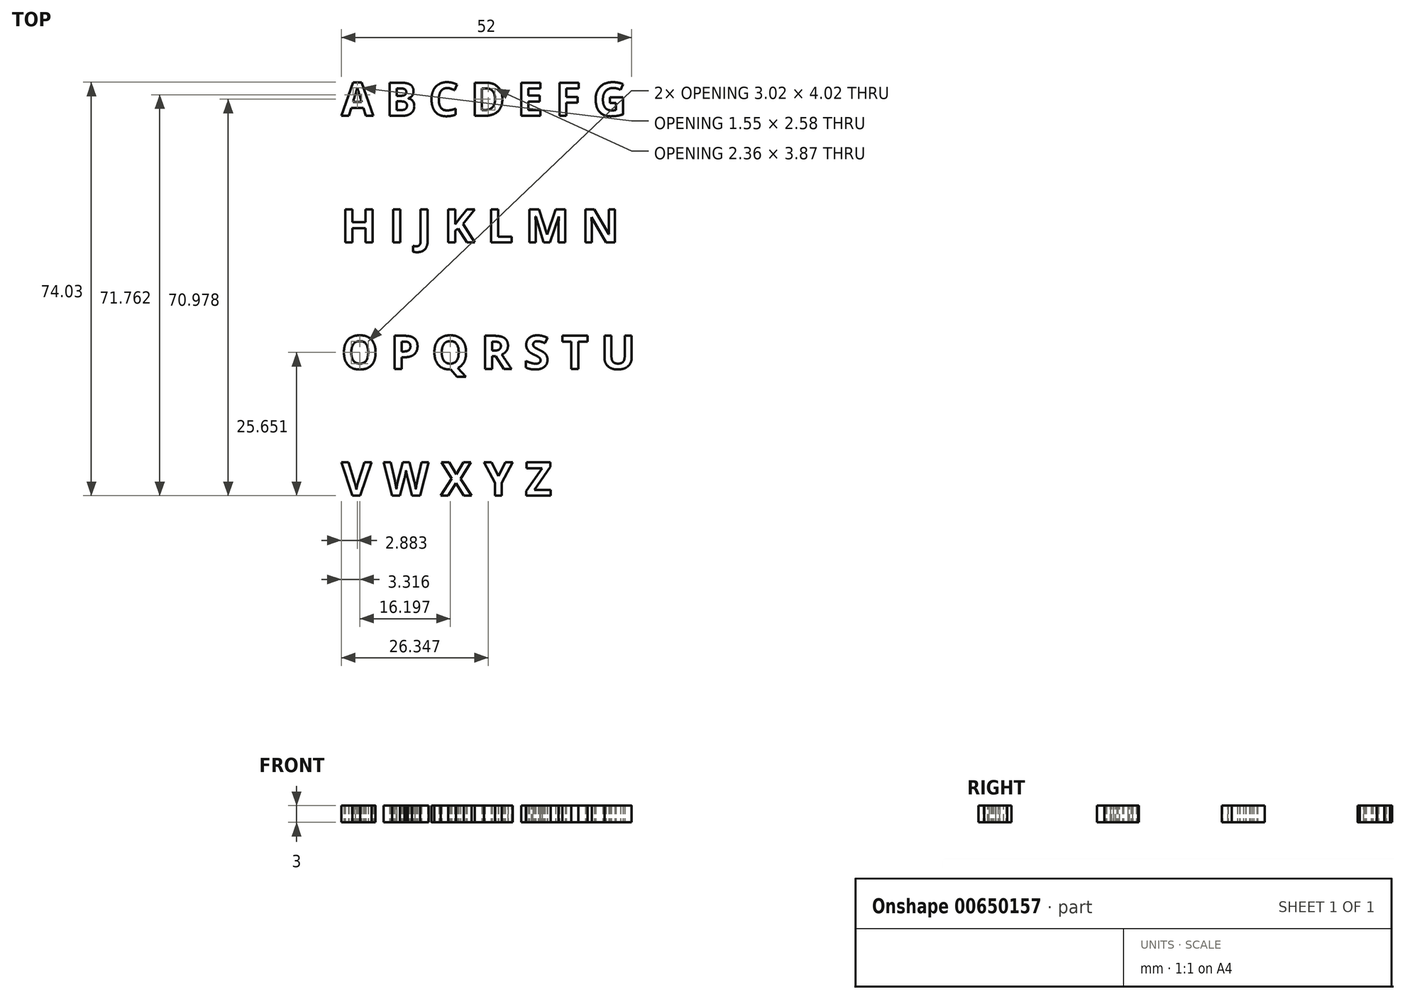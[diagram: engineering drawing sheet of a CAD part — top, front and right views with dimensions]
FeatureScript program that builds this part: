
annotation { "Feature Type Name" : "Feature", "Feature Type Description" : "" }
export const myFeature = defineFeature(function(context is Context, id is Id, definition is map)
    precondition{}
    {
        {
            var Q0;
            Q0=qCreatedBy(makeId("Top.planeOp"),FACE);
            var sketch = newSketch(context, id + "F0", { "sketchPlane" : qUnion([Q0])});
            skPoint(sketch, "E0.middle", {"position": v(-24.74, 7.18) * mm});
            skText(sketch, "E1", { "text": "A B C D E F G \n\nH I J K L M N\n\nO P Q R S T U\n\nV W X Y Z ", "fontName": "OpenSans-Bold.ttf"});
            const initialGuessF0  = {"E1": [-0.06653, 0.0315, 1, 0, 0.006]};
            skSetInitialGuess(sketch, initialGuessF0);
            skSolve(sketch);
        }
        {
            var Q0;
            Q0 = qSketchRegion(id + "F0", true);
            extrude(context, id + "F1", {"entities" : qUnion([Q0]), "depth" : 3 * mm, "offsetDistance" : 25 * mm});
        }
    });
